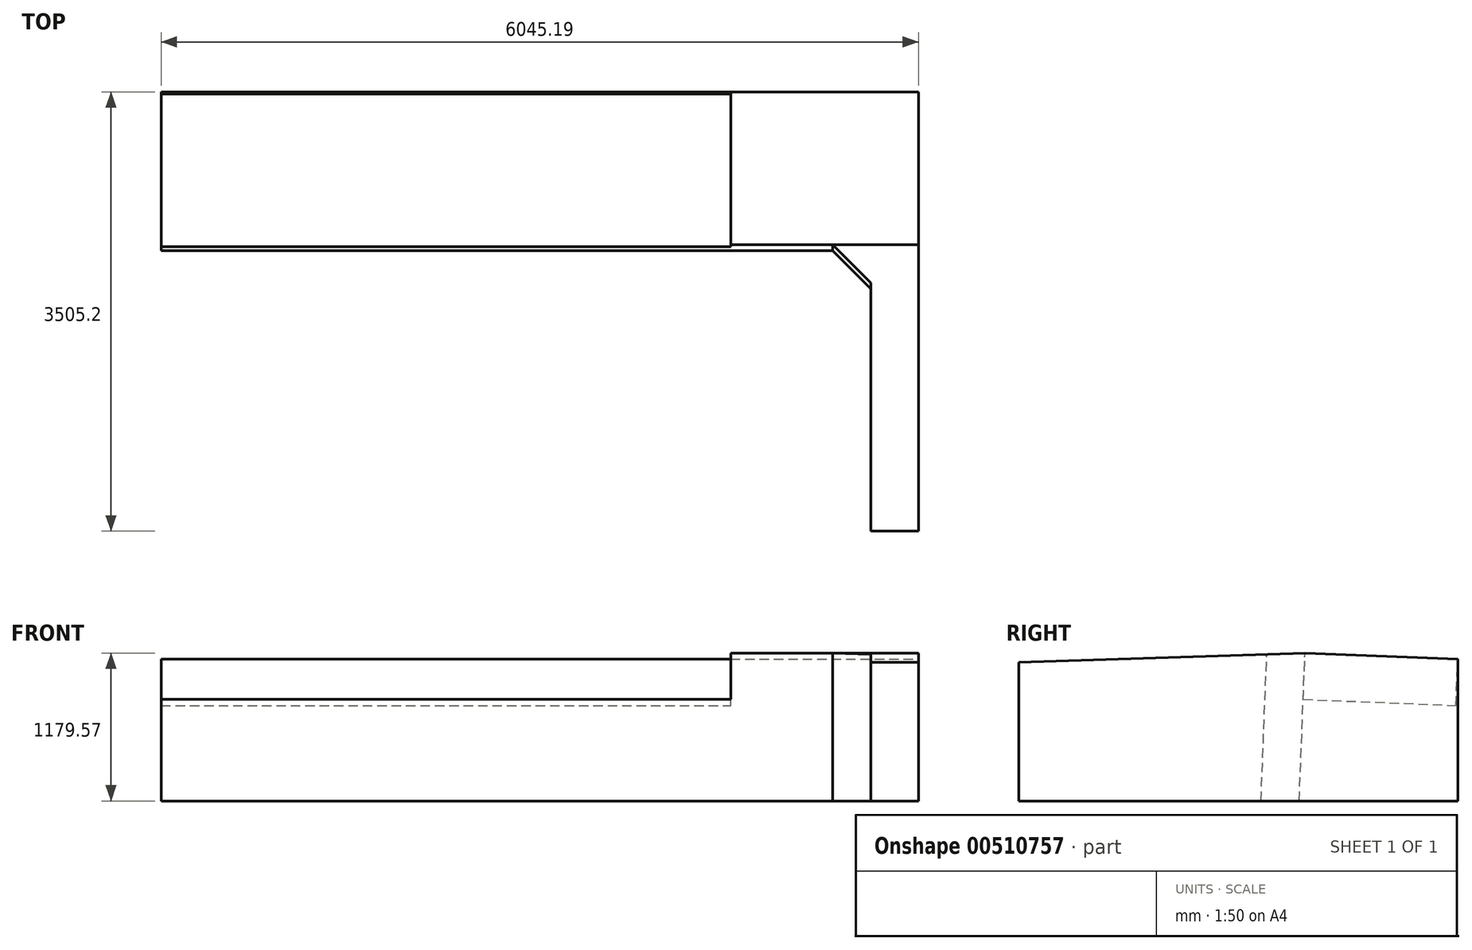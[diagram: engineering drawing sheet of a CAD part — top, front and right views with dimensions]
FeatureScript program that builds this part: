
annotation { "Feature Type Name" : "Feature", "Feature Type Description" : "" }
export const myFeature = defineFeature(function(context is Context, id is Id, definition is map)
    precondition{}
    {
        {
            var Q0;
            Q0=qCreatedBy(makeId("Right.planeOp"),FACE);
            var sketch = newSketch(context, id + "F0", { "sketchPlane" : qUnion([Q0])});
            skLineSegment(sketch, "E0", {"start": v(0, 1484.38) * mm, "end": v(-3505.2, 1484.38) * mm});
            skLineSegment(sketch, "E1", {"start": v(-3505.2, 1484.38) * mm, "end": v(-3505.2, 2590.8) * mm});
            skLineSegment(sketch, "E2", {"start": v(-3505.2, 2590.8) * mm, "end": v(-1219.2, 2663.95) * mm});
            skLineSegment(sketch, "E3", {"start": v(-1219.2, 2663.95) * mm, "end": v(0, 2615.18) * mm});
            skLineSegment(sketch, "E4", {"start": v(0, 2615.18) * mm, "end": v(0, 1484.38) * mm});
            skSolve(sketch);
        }
        {
            var Q0;
            Q0=qCreatedBy(makeId("Right.planeOp"),FACE);
            cPlane(context, id + "F1", {"entities" : qUnion([Q0]), "cplaneType" : CPlaneType.OFFSET, "offset" : 12115.8 * mm, "oppositeDirection" : true, "width" : 152.4 * mm, "height" : 152.4 * mm});
        }
        {
            var Q0;
            Q0=makeQuery(id+"F0.imprint","IMPRINT",FACE,{"disambiguationData":[TD([[makeQuery(id+"F0.imprint","IMPRINT",EDGE,{"derivedFrom":sQuery(id+"F0.wireOp",EDGE,"E0")}),-1.0]])]});
            extrude(context, id + "F2", {"entities" : qUnion([Q0]), "oppositeDirection" : true, "depth" : 6045.19 * mm});
        }
        {
            var Q0;
            Q0=makeQuery(id+"F2.opExtrude","SWEPT_FACE",FACE,{"disambiguationData":[OSD([sQuery(id+"F0.wireOp",EDGE,"E3")])]});
            var sketch = newSketch(context, id + "F3", { "sketchPlane" : qUnion([Q0])});
            skLineSegment(sketch, "E5", {"start": v(-6045.19, -1324.7) * mm, "end": v(-685.8, -1324.7) * mm});
            skLineSegment(sketch, "E6", {"start": v(-685.8, -1324.7) * mm, "end": v(-381, -1629.5) * mm});
            skLineSegment(sketch, "E7", {"start": v(-381, -1629.5) * mm, "end": v(-381, -3610.7) * mm});
            skLineSegment(sketch, "E8", {"start": v(-381, -3610.7) * mm, "end": v(-6045.19, -3610.7) * mm});
            skLineSegment(sketch, "E9", {"start": v(-6045.19, -3610.7) * mm, "end": v(-6045.19, -1324.7) * mm});
            skSolve(sketch);
        }
        {
            var Q0;
            Q0 = qSketchRegion(id + "F3", true);
            extrude(context, id + "F4", {"entities" : qUnion([Q0]), "operationType" : NewBodyOperationType.REMOVE, "endBound" : BoundingType.THROUGH_ALL, "oppositeDirection" : true, "depth" : 30.48 * mm});
        }
        {
            var Q0;
            Q0=makeQuery(id+"F2.opExtrude","SWEPT_FACE",FACE,{"disambiguationData":[OSD([sQuery(id+"F0.wireOp",EDGE,"E3")])]});
            var sketch = newSketch(context, id + "F5", { "sketchPlane" : qUnion([Q0])});
            skLineSegment(sketch, "E10.bottom", {"start": v(-6045.19, -104.52) * mm, "end": v(-1498.6, -104.52) * mm});
            skLineSegment(sketch, "E10.top", {"start": v(-6045.19, -1324.7) * mm, "end": v(-1498.6, -1324.7) * mm});
            skLineSegment(sketch, "E10.left", {"start": v(-6045.19, -104.52) * mm, "end": v(-6045.19, -1324.7) * mm});
            skLineSegment(sketch, "E10.right", {"start": v(-1498.6, -104.52) * mm, "end": v(-1498.6, -1324.7) * mm});
            skSolve(sketch);
        }
        {
            var Q0;
            Q0 = qSketchRegion(id + "F5", true);
            extrude(context, id + "F6", {"entities" : qUnion([Q0]), "operationType" : NewBodyOperationType.REMOVE, "oppositeDirection" : true, "depth" : 368.8 * mm});
        }
    });
